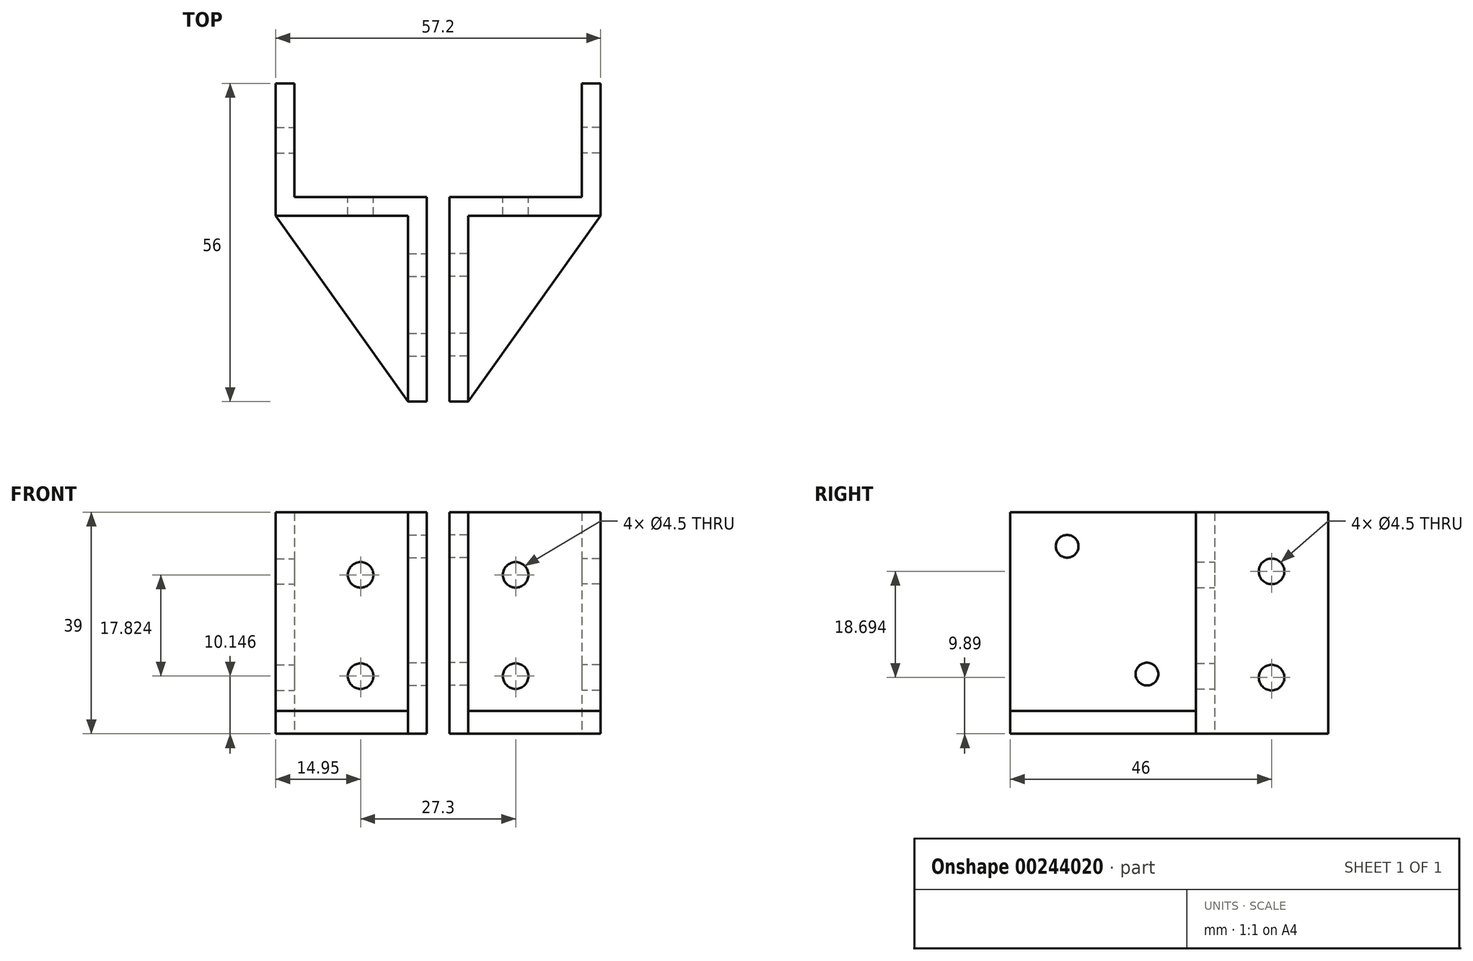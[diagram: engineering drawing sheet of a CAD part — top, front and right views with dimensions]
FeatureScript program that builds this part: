
annotation { "Feature Type Name" : "Feature", "Feature Type Description" : "" }
export const myFeature = defineFeature(function(context is Context, id is Id, definition is map)
    precondition{}
    {
        {
            var Q0;
            Q0=qCreatedBy(makeId("Top.planeOp"),FACE);
            var sketch = newSketch(context, id + "F0", { "sketchPlane" : qUnion([Q0])});
            skLineSegment(sketch, "E0", {"start": v(5.3, -36) * mm, "end": v(28.6, -3.3) * mm});
            skLineSegment(sketch, "E1", {"start": v(28.6, -3.3) * mm, "end": v(28.6, 0) * mm});
            skLineSegment(sketch, "E2", {"start": v(28.6, 0) * mm, "end": v(28.6, 20) * mm});
            skLineSegment(sketch, "E3", {"start": v(28.6, 20) * mm, "end": v(25.3, 20) * mm});
            skLineSegment(sketch, "E4", {"start": v(25.3, 20) * mm, "end": v(25.3, 0) * mm});
            skLineSegment(sketch, "E5", {"start": v(25.3, 0) * mm, "end": v(2, 0) * mm});
            skLineSegment(sketch, "E6", {"start": v(2, 0) * mm, "end": v(2, -36) * mm});
            skLineSegment(sketch, "E7", {"start": v(2, -36) * mm, "end": v(5.3, -36) * mm});
            skSolve(sketch);
        }
        {
            var Q0;
            Q0=makeQuery(id+"F0.imprint","IMPRINT",FACE,{"disambiguationData":[TD([[makeQuery(id+"F0.imprint","IMPRINT",EDGE,{"derivedFrom":sQuery(id+"F0.wireOp",EDGE,"E0")}),1.0]])]});
            extrude(context, id + "F1", {"entities" : qUnion([Q0]), "depth" : 4 * mm});
        }
        {
            var Q0;
            Q0=makeQuery(id+"F1.opExtrude","CAP_FACE",FACE,{"disambiguationData":[OSD([sQuery(id+"F0.wireOp",EDGE,"ge1uVfWQ-8EBl-40up-Tlfm-gRpWl6JdF0Np"),sQuery(id+"F0.wireOp",EDGE,"RATsxs2y-CiEd-F7bT-hT3x-qLXvmSWZdbcS"),sQuery(id+"F0.wireOp",EDGE,"E0"),sQuery(id+"F0.wireOp",EDGE,"E1"),sQuery(id+"F0.wireOp",EDGE,"E2"),sQuery(id+"F0.wireOp",EDGE,"E3"),sQuery(id+"F0.wireOp",EDGE,"E4"),sQuery(id+"F0.wireOp",EDGE,"E5")])],"isStart":false});
            var sketch = newSketch(context, id + "F2", { "sketchPlane" : qUnion([Q0])});
            skLineSegment(sketch, "E8", {"start": v(5.3, -36) * mm, "end": v(5.3, -3.3) * mm});
            skLineSegment(sketch, "E9", {"start": v(5.3, -3.3) * mm, "end": v(28.6, -3.3) * mm});
            skSolve(sketch);
        }
        {
            var Q0;
            Q0=makeQuery(id+"F2.imprint","IMPRINT",FACE,{"disambiguationData":[TD([[makeQuery(id+"F2.imprint","IMPRINT",EDGE,{"derivedFrom":sQuery(id+"F2.wireOp",EDGE,"E8")}),1.0]])]});
            extrude(context, id + "F3", {"entities" : qUnion([Q0]), "operationType" : NewBodyOperationType.ADD, "depth" : 35 * mm});
        }
        {
            var Q0;
            {var subQ0=sQuery(id+"F0.wireOp",EDGE,"E4");Q0=makeQuery(id+"F3.boolean.opBoolean","MERGE",FACE,{"derivedFrom":[makeQuery(id+"F1.opExtrude","SWEPT_FACE",FACE,{"disambiguationData":[OSD([subQ0])]}),makeQuery(id+"F3.opExtrude","SWEPT_FACE",FACE,{"disambiguationData":[OSD([subQ0])]})]});}
            var sketch = newSketch(context, id + "F4", { "sketchPlane" : qUnion([Q0])});
            skLineSegment(sketch, "E10", {"start": v(-10, 43.94) * mm, "end": v(-10, -2.24) * mm, "construction": true});
            skPoint(sketch, "E10.startSnap0", {"position": v(-10, 39) * mm});
            skPoint(sketch, "E10.endSnap0", {"position": v(-10, 0) * mm});
            skCircle(sketch, "E11", {"center": v(-10, 28.58) * mm, "radius": 2.25 * mm});
            skCircle(sketch, "E12", {"center": v(-10, 9.9) * mm, "radius": 2.25 * mm});
            skSolve(sketch);
        }
        {
            var Q0;
            Q0=makeQuery(id+"F4.imprint","IMPRINT",FACE,{"disambiguationData":[TD([[makeQuery(id+"F4.imprint","IMPRINT",EDGE,{"derivedFrom":sQuery(id+"F4.wireOp",EDGE,"E11")}),1.0]])]});
            var Q1;
            Q1=makeQuery(id+"F4.imprint","IMPRINT",FACE,{"disambiguationData":[TD([[makeQuery(id+"F4.imprint","IMPRINT",EDGE,{"derivedFrom":sQuery(id+"F4.wireOp",EDGE,"E12")}),1.0]])]});
            extrude(context, id + "F5", {"entities" : qUnion([Q0, Q1]), "operationType" : NewBodyOperationType.REMOVE, "endBound" : BoundingType.UP_TO_NEXT, "oppositeDirection" : true, "depth" : 25 * mm});
        }
        {
            var Q0;
            {var subQ0=sQuery(id+"F0.wireOp",EDGE,"E6");Q0=makeQuery(id+"F3.boolean.opBoolean","MERGE",FACE,{"derivedFrom":[makeQuery(id+"F1.opExtrude","SWEPT_FACE",FACE,{"disambiguationData":[OSD([subQ0])]}),makeQuery(id+"F3.opExtrude","SWEPT_FACE",FACE,{"disambiguationData":[OSD([subQ0])]})]});}
            var sketch = newSketch(context, id + "F6", { "sketchPlane" : qUnion([Q0])});
            skLineSegment(sketch, "E13", {"start": v(26, 43.9) * mm, "end": v(26, -5.51) * mm, "construction": true});
            skLineSegment(sketch, "E14", {"start": v(12, 44.58) * mm, "end": v(12, -6.2) * mm, "construction": true});
            skLineSegment(sketch, "E15", {"start": v(21.65, 33) * mm, "end": v(31.55, 33) * mm, "construction": true});
            skCircle(sketch, "E16", {"center": v(26, 33) * mm, "radius": 2 * mm});
            skLineSegment(sketch, "E17", {"start": v(5.53, 10.5) * mm, "end": v(18.35, 10.5) * mm, "construction": true});
            skCircle(sketch, "E18", {"center": v(11.94, 10.5) * mm, "radius": 2 * mm});
            skSolve(sketch);
        }
        {
            var Q0;
            Q0=makeQuery(id+"F6.imprint","IMPRINT",FACE,{"disambiguationData":[TD([[makeQuery(id+"F6.imprint","IMPRINT",EDGE,{"derivedFrom":sQuery(id+"F6.wireOp",EDGE,"E16")}),1.0]])]});
            var Q1;
            Q1=makeQuery(id+"F6.imprint","IMPRINT",FACE,{"disambiguationData":[TD([[makeQuery(id+"F6.imprint","IMPRINT",EDGE,{"derivedFrom":sQuery(id+"F6.wireOp",EDGE,"E18")}),1.0]])]});
            extrude(context, id + "F7", {"entities" : qUnion([Q0, Q1]), "operationType" : NewBodyOperationType.REMOVE, "endBound" : BoundingType.UP_TO_NEXT, "oppositeDirection" : true, "depth" : 25 * mm});
        }
        {
            var Q0;
            {var subQ0=sQuery(id+"F0.wireOp",EDGE,"E5");Q0=makeQuery(id+"F3.boolean.opBoolean","MERGE",FACE,{"derivedFrom":[makeQuery(id+"F1.opExtrude","SWEPT_FACE",FACE,{"disambiguationData":[OSD([subQ0])]}),makeQuery(id+"F3.opExtrude","SWEPT_FACE",FACE,{"disambiguationData":[OSD([subQ0])]})]});}
            var sketch = newSketch(context, id + "F8", { "sketchPlane" : qUnion([Q0])});
            skLineSegment(sketch, "E19", {"start": v(-13.65, 40.99) * mm, "end": v(-13.65, -2.26) * mm, "construction": true});
            skPoint(sketch, "E19.startSnap0", {"position": v(-13.65, 39) * mm});
            skPoint(sketch, "E19.endSnap0", {"position": v(-13.65, 0) * mm});
            skCircle(sketch, "E20", {"center": v(-13.65, 27.97) * mm, "radius": 2.25 * mm});
            skCircle(sketch, "E21", {"center": v(-13.65, 10.15) * mm, "radius": 2.25 * mm});
            skSolve(sketch);
        }
        {
            var Q0;
            Q0=makeQuery(id+"F8.imprint","IMPRINT",FACE,{"disambiguationData":[TD([[makeQuery(id+"F8.imprint","IMPRINT",EDGE,{"derivedFrom":sQuery(id+"F8.wireOp",EDGE,"E20")}),1.0]])]});
            var Q1;
            Q1=makeQuery(id+"F8.imprint","IMPRINT",FACE,{"disambiguationData":[TD([[makeQuery(id+"F8.imprint","IMPRINT",EDGE,{"derivedFrom":sQuery(id+"F8.wireOp",EDGE,"E21")}),1.0]])]});
            extrude(context, id + "F9", {"entities" : qUnion([Q0, Q1]), "operationType" : NewBodyOperationType.REMOVE, "endBound" : BoundingType.UP_TO_NEXT, "oppositeDirection" : true, "depth" : 25 * mm});
        }
        {
            var Q0;
            Q0=makeQuery(id+"F1.opExtrude","SWEPT_BODY",BODY,{"disambiguationData":[OSD([sQuery(id+"F0.wireOp",EDGE,"ge1uVfWQ-8EBl-40up-Tlfm-gRpWl6JdF0Np"),sQuery(id+"F0.wireOp",EDGE,"RATsxs2y-CiEd-F7bT-hT3x-qLXvmSWZdbcS"),sQuery(id+"F0.wireOp",EDGE,"E0"),sQuery(id+"F0.wireOp",EDGE,"E1"),sQuery(id+"F0.wireOp",EDGE,"E2"),sQuery(id+"F0.wireOp",EDGE,"E3"),sQuery(id+"F0.wireOp",EDGE,"E4"),sQuery(id+"F0.wireOp",EDGE,"E5")])]});
            var Q1;
            Q1=qCreatedBy(makeId("Right.planeOp"),FACE);
            mirror(context, id + "F10", {"operationType" : NewBodyOperationType.ADD, "entities" : qUnion([Q0]), "mirrorPlane" : qUnion([Q1])});
        }
    });
